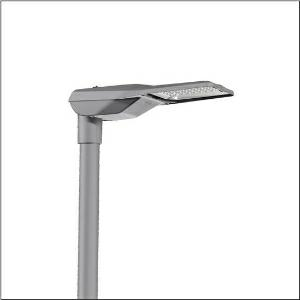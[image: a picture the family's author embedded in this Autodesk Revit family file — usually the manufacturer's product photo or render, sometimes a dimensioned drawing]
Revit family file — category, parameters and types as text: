
# Revit family: streetlight_sl_21_mini___stw1_0a_5xe2e43s08jb_a2c1
name_source: partatom
category: Lighting Fixtures
units: mm (PartAtom-declared; Revit-internal decimal feet)

## family parameters
Cut with Voids When Loaded = No
Host = Face
Light Source = No
Part Type = Normal
Room Calculation Point = No
Round Connector Dimension = Use Diameter
Shared = No

## types (1)
- --- (1 x LED, 13500 lm, 88.6 W, 4000K)
    Apparent Load = 89 VA
    CIE Flux Codes = 39 75 98 100 100
    Color Rendering = 70
    Color Temperature = 4000K
    Default Elevation = 1800 mm
    Description = Streetlight SL 21 mini, mast luminaire, primary light control with lens, of PMMA, primary optical cover: cover, of toughened safety glass, transparent, light distribution: STW1.0a, light emission: direct distribution, primary light characteristic: asymmetric, installation type: side-entry, post-top, LED, High Power LED, rated luminous flux: 13.500lm, luminous efficacy: 152lm/W, light colour: 740, colour temperature: 4000K, control gear: D4i, control: overheat protection, constant luminous flux control, time-dependent luminous flux control, flexible luminous flux parameterisation, pre-setting: logarithmic dimming characteristic, mains connection: 220..240V, AC, 50/60Hz, start of lifetime: 89W, end of service life: 92W, reduction: 41W, luminaire housing, of diecast aluminium, powder-coated, SITECO metallic grey (DB 702S), corrosivity category C5 high according to DIN EN ISO 12944, please order mast flange separately, inclination adjustable: 0°, 5°, 10°, 15°, sealing non-destructively replaceable, multi-level sealing system, length: 628mm, width: 235mm, height: 110mm, mast flange for spigot size: 42mm (side-entry): 5XC10008XM4, 60/48mm (side-entry/post-top): 5XC10108XM2, 76/60mm (side-entry/post-top): 5XC10108XM1, mounting height: 4..8m, Smart Interface above, protection rating (complete): IP66, insulation class (complete): insulation class II (safety insulation), certification: CE, ENEC, ENEC+, VDE, impact resistance: IK10, permissible operating ambient temperature for outdoor applications: -40..+50°C, standard-compliant lighting for roads and squares, packaging unit: 1 piece

Light Distribution: STW1.0a
    Height = 110 mm
    Lamp = 1 x LED
    Lamp Light Flux = 13500 lm
    Lamp Power = 88.6 W
    Lamp count = 1
    Length = 625 mm
    Luminous efficacy = 152 lm/W
    Manufacturer = Siteco
    ModVariant = No
    Model = 5XE2E43S08JB
    Number of Poles = 1
    OnlyDefault = Yes
    Power Factor = 1
    Product Name = Streetlight SL 21 mini | STW1.0a
    Product group = mast luminaire | pylon top
    ProductGroupID = 6100
    Protection Class = Protection class II
    Protection Degree = IP 66
    RLX_Detail_Level = 1
    RLX_Emergency_Light_Flux = 0 lm
    RLX_Emergency_Type = 0
    RLX_Emergency_Type_DB = No
    RlxData = <blob elided: 26281 chars, md5=b1ffa603>
    Socket = socket
    Standby Power = 0 W
    System Light Flux = 13500 lm
    System Power = 89 W
    Type Comments = factory setting: luminous flux: 100 % | dim-lin: 254 | 915 mA
    Type Image = l_1003515.jpg
    URL = http://relux.com
    VarID = @adj_031197
    Voltage = 0 V
    Weight = 0.00 kg
    Width = 234 mm

## geometry (parser evidence)
native form markers: Blend x4, Sweep x12
no freeform markers — native parametric forms only
